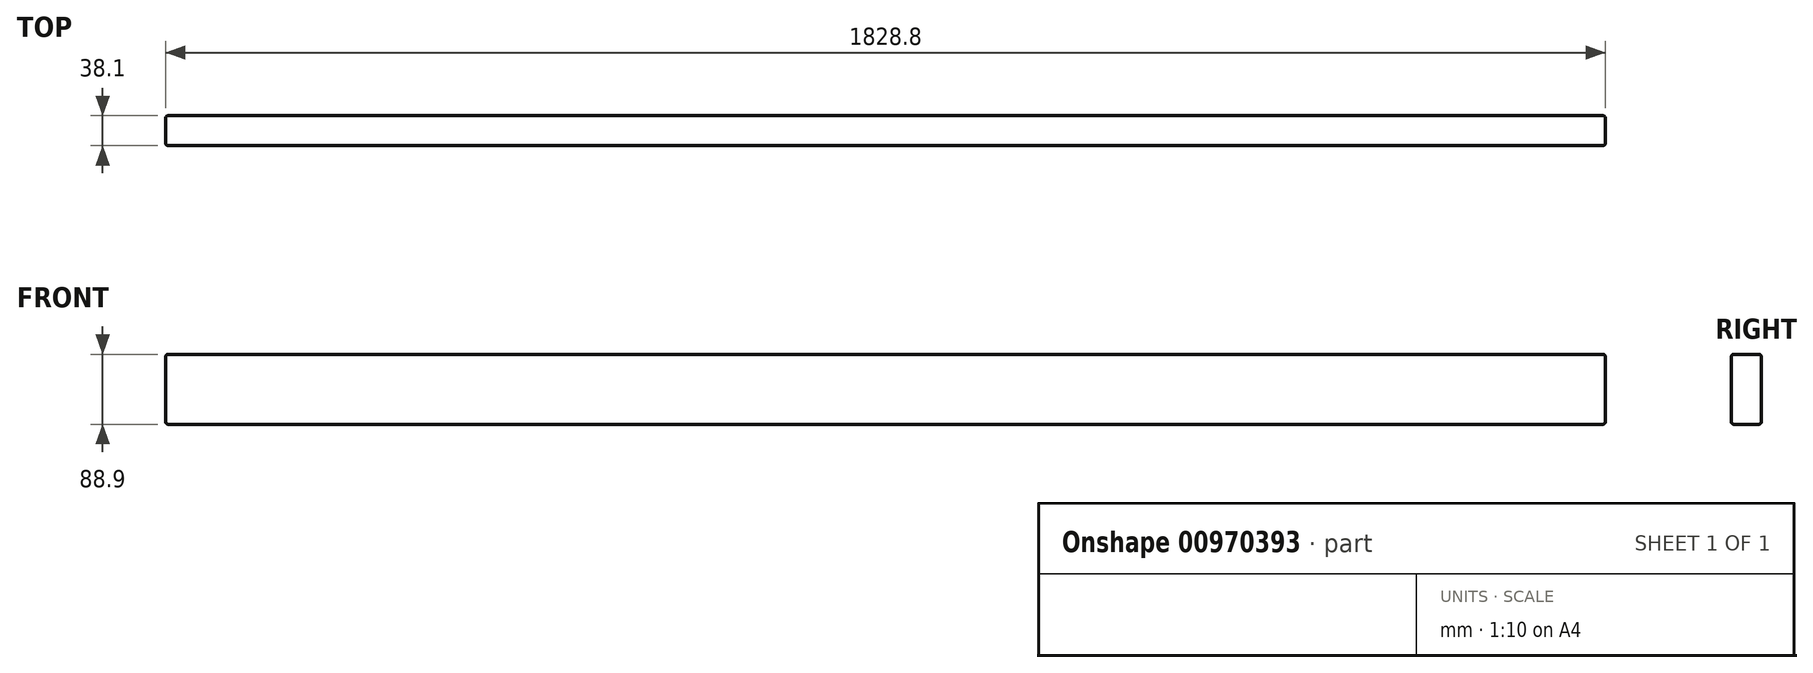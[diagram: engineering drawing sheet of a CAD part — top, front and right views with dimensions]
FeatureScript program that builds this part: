
annotation { "Feature Type Name" : "Feature", "Feature Type Description" : "" }
export const myFeature = defineFeature(function(context is Context, id is Id, definition is map)
    precondition{}
    {
        {
            var Q0;
            Q0=qCreatedBy(makeId("Front.planeOp"),FACE);
            var sketch = newSketch(context, id + "F0", { "sketchPlane" : qUnion([Q0])});
            skLineSegment(sketch, "E0.bottom", {"start": v(1828.8, 0) * mm, "end": v(0, 0) * mm});
            skLineSegment(sketch, "E0.top", {"start": v(1828.8, -88.9) * mm, "end": v(0, -88.9) * mm});
            skLineSegment(sketch, "E0.left", {"start": v(1828.8, 0) * mm, "end": v(1828.8, -88.9) * mm});
            skLineSegment(sketch, "E0.right", {"start": v(0, 0) * mm, "end": v(0, -88.9) * mm});
            skSolve(sketch);
        }
        {
            var Q0;
            Q0=makeQuery(id+"F0.imprint","IMPRINT",FACE,{"disambiguationData":[TD([[makeQuery(id+"F0.imprint","IMPRINT",EDGE,{"derivedFrom":sQuery(id+"F0.wireOp",EDGE,"E0.bottom")}),1.0]])]});
            extrude(context, id + "F1", {"entities" : qUnion([Q0]), "depth" : 38.1 * mm, "offsetDistance" : 25.4 * mm});
        }
        {
            var Q0;
            Q0=makeQuery(id+"F1.opExtrude","CAP_EDGE",EDGE,{"disambiguationData":[OSD([sQuery(id+"F0.wireOp",EDGE,"E0.bottom")])],"isStart":false});
            var Q1;
            Q1=makeQuery(id+"F1.opExtrude","CAP_EDGE",EDGE,{"disambiguationData":[OSD([sQuery(id+"F0.wireOp",EDGE,"E0.bottom")])],"isStart":true});
            var Q2;
            Q2=makeQuery(id+"F1.opExtrude","CAP_EDGE",EDGE,{"disambiguationData":[OSD([sQuery(id+"F0.wireOp",EDGE,"E0.top")])],"isStart":false});
            var Q3;
            Q3=makeQuery(id+"F1.opExtrude","CAP_EDGE",EDGE,{"disambiguationData":[OSD([sQuery(id+"F0.wireOp",EDGE,"E0.right")])],"isStart":false});
            var Q4;
            Q4=makeQuery(id+"F1.opExtrude","SWEPT_EDGE",EDGE,{"disambiguationData":[OSD([sQuery(id+"F0.wireOp",EDGE,"E0.bottom"),sQuery(id+"F0.wireOp",EDGE,"E0.right")])]});
            var Q5;
            Q5=makeQuery(id+"F1.opExtrude","SWEPT_EDGE",EDGE,{"disambiguationData":[OSD([sQuery(id+"F0.wireOp",EDGE,"E0.top"),sQuery(id+"F0.wireOp",EDGE,"E0.right")])]});
            var Q6;
            Q6=makeQuery(id+"F1.opExtrude","CAP_EDGE",EDGE,{"disambiguationData":[OSD([sQuery(id+"F0.wireOp",EDGE,"E0.right")])],"isStart":true});
            var Q7;
            Q7=makeQuery(id+"F1.opExtrude","CAP_EDGE",EDGE,{"disambiguationData":[OSD([sQuery(id+"F0.wireOp",EDGE,"E0.top")])],"isStart":true});
            var Q8;
            Q8=makeQuery(id+"F1.opExtrude","SWEPT_EDGE",EDGE,{"disambiguationData":[OSD([sQuery(id+"F0.wireOp",EDGE,"E0.top"),sQuery(id+"F0.wireOp",EDGE,"E0.left")])]});
            var Q9;
            Q9=makeQuery(id+"F1.opExtrude","CAP_EDGE",EDGE,{"disambiguationData":[OSD([sQuery(id+"F0.wireOp",EDGE,"E0.left")])],"isStart":false});
            var Q10;
            Q10=makeQuery(id+"F1.opExtrude","SWEPT_EDGE",EDGE,{"disambiguationData":[OSD([sQuery(id+"F0.wireOp",EDGE,"E0.bottom"),sQuery(id+"F0.wireOp",EDGE,"E0.left")])]});
            var Q11;
            Q11=makeQuery(id+"F1.opExtrude","CAP_EDGE",EDGE,{"disambiguationData":[OSD([sQuery(id+"F0.wireOp",EDGE,"E0.left")])],"isStart":true});
            fillet(context, id + "F2", {"entities" : qUnion([Q0, Q1, Q2, Q3, Q4, Q5, Q6, Q7, Q8, Q9, Q10, Q11]), "radius" : 3.17 * mm, "tangentPropagation" : true, "allowEdgeOverflow" : false});
        }
    });
